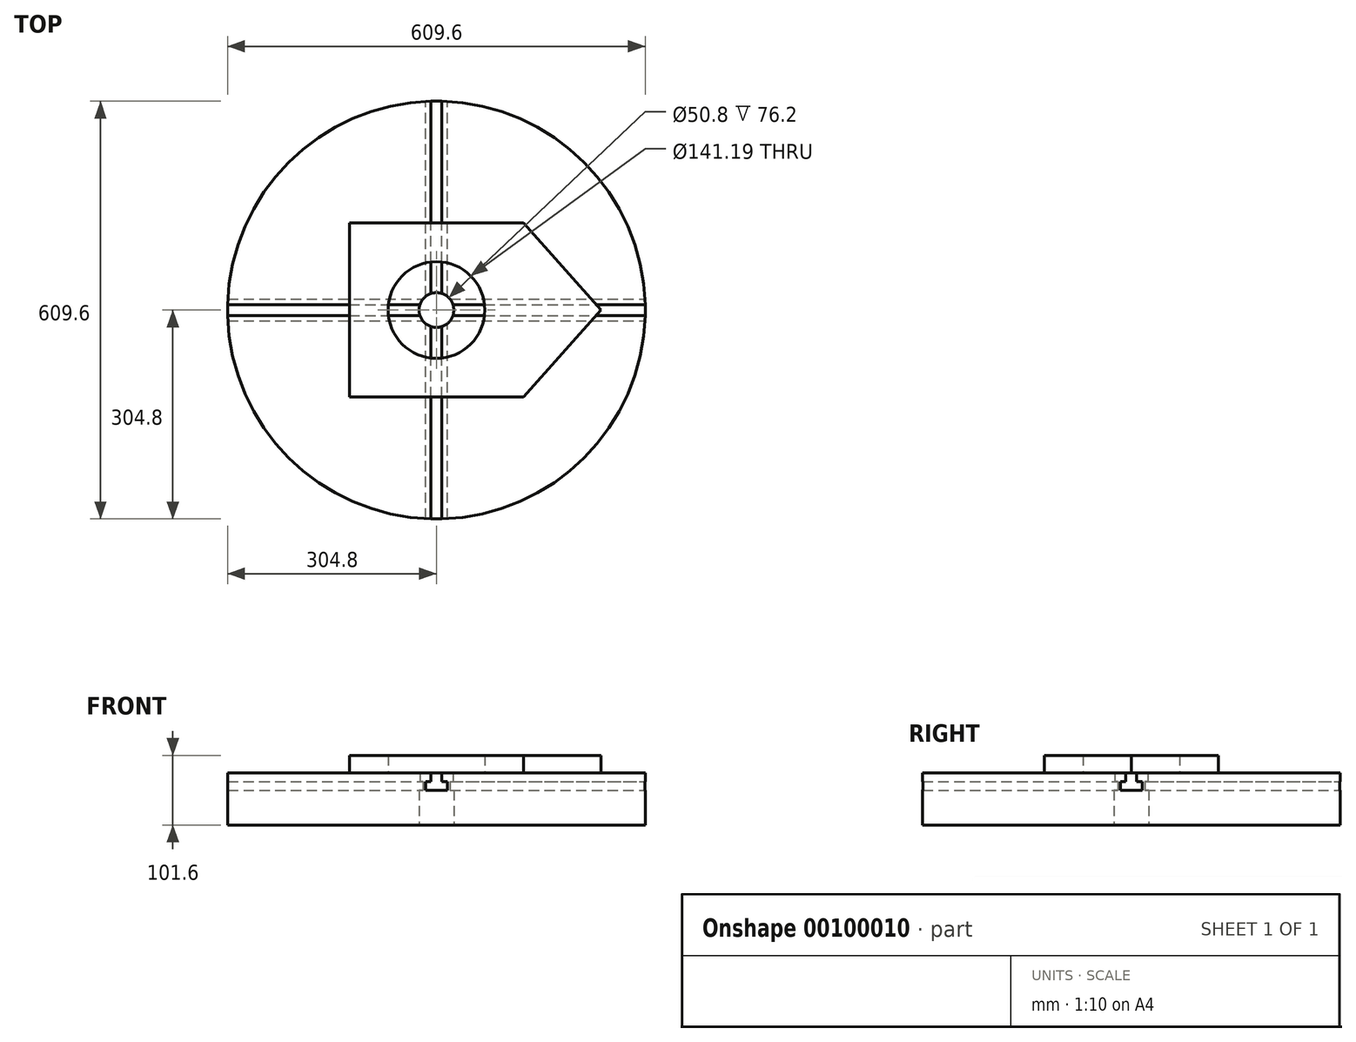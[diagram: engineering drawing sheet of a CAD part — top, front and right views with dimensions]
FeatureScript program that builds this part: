
annotation { "Feature Type Name" : "Feature", "Feature Type Description" : "" }
export const myFeature = defineFeature(function(context is Context, id is Id, definition is map)
    precondition{}
    {
        {
            var Q0;
            Q0=qCreatedBy(makeId("Top.planeOp"),FACE);
            var sketch = newSketch(context, id + "F0", { "sketchPlane" : qUnion([Q0])});
            skCircle(sketch, "E0", {"center": v(0, 0) * mm, "radius": 304.8 * mm});
            skCircle(sketch, "E1", {"center": v(0, 0) * mm, "radius": 25.4 * mm});
            skSolve(sketch);
        }
        {
            var Q0;
            Q0=qSketchRegion(id+"F0",true);
            extrude(context, id + "F1", {"entities" : qUnion([Q0]), "depth" : 76.2 * mm});
        }
        {
            var Q0;
            Q0=qCreatedBy(makeId("Front.planeOp"),FACE);
            var sketch = newSketch(context, id + "F2", { "sketchPlane" : qUnion([Q0])});
            skLineSegment(sketch, "E2", {"start": v(-7.94, 76.2) * mm, "end": v(-7.94, 63.5) * mm});
            skLineSegment(sketch, "E3", {"start": v(-7.94, 63.5) * mm, "end": v(-15.88, 63.5) * mm});
            skLineSegment(sketch, "E4", {"start": v(-15.88, 63.5) * mm, "end": v(-15.88, 50.8) * mm});
            skLineSegment(sketch, "E5", {"start": v(-15.88, 50.8) * mm, "end": v(15.88, 50.8) * mm});
            skLineSegment(sketch, "E6", {"start": v(15.88, 50.8) * mm, "end": v(15.88, 63.5) * mm});
            skLineSegment(sketch, "E7", {"start": v(15.88, 63.5) * mm, "end": v(7.94, 63.5) * mm});
            skLineSegment(sketch, "E8", {"start": v(7.94, 63.5) * mm, "end": v(7.94, 76.2) * mm});
            skLineSegment(sketch, "E9", {"start": v(7.94, 76.2) * mm, "end": v(-7.94, 76.2) * mm});
            skLineSegment(sketch, "E10", {"start": v(0, 0) * mm, "end": v(0, 117.73) * mm, "construction": true});
            skSolve(sketch);
        }
        {
            var Q0;
            Q0=makeQuery(id+"F2.imprint","IMPRINT",FACE,{"disambiguationData":[TD([[makeQuery(id+"F2.imprint","IMPRINT",EDGE,{"derivedFrom":sQuery(id+"F2.wireOp",EDGE,"E2")}),1.0]])]});
            extrude(context, id + "F3", {"entities" : qUnion([Q0]), "endBound" : BoundingType.THROUGH_ALL, "depth" : 25.4 * mm, "hasSecondDirection" : true, "secondDirectionBound" : SecondDirectionBoundingType.THROUGH_ALL, "secondDirectionOppositeDirection" : true, "secondDirectionDepth" : 25.4 * mm});
        }
        {
            var Q0;
            Q0=makeQuery(id+"F3.opExtrude","SWEPT_BODY",BODY,{"disambiguationData":[OSD([sQuery(id+"F2.wireOp",EDGE,"E2"),sQuery(id+"F2.wireOp",EDGE,"E3"),sQuery(id+"F2.wireOp",EDGE,"E4"),sQuery(id+"F2.wireOp",EDGE,"E5"),sQuery(id+"F2.wireOp",EDGE,"E6"),sQuery(id+"F2.wireOp",EDGE,"E7"),sQuery(id+"F2.wireOp",EDGE,"E8"),sQuery(id+"F2.wireOp",EDGE,"E9")])]});
            var Q1;
            Q1=sQuery(id+"F2.wireOp",EDGE,"E10");
            circularPattern(context, id + "F4", {"entities" : qUnion([Q0]), "axis" : qUnion([Q1]), "angle" : 90 * degree, "instanceCount" : 2});
        }
        {
            var Q0;
            Q0=makeQuery(id+"F4.opPattern","COPY",BODY,{"derivedFrom":makeQuery(id+"F3.opExtrude","SWEPT_BODY",BODY,{"disambiguationData":[OSD([sQuery(id+"F2.wireOp",EDGE,"E2"),sQuery(id+"F2.wireOp",EDGE,"E3"),sQuery(id+"F2.wireOp",EDGE,"E4"),sQuery(id+"F2.wireOp",EDGE,"E5"),sQuery(id+"F2.wireOp",EDGE,"E6"),sQuery(id+"F2.wireOp",EDGE,"E7"),sQuery(id+"F2.wireOp",EDGE,"E8"),sQuery(id+"F2.wireOp",EDGE,"E9")])]}),"instanceName":"1"});
            var Q1;
            Q1=makeQuery(id+"F3.opExtrude","SWEPT_BODY",BODY,{"disambiguationData":[OSD([sQuery(id+"F2.wireOp",EDGE,"E2"),sQuery(id+"F2.wireOp",EDGE,"E3"),sQuery(id+"F2.wireOp",EDGE,"E4"),sQuery(id+"F2.wireOp",EDGE,"E5"),sQuery(id+"F2.wireOp",EDGE,"E6"),sQuery(id+"F2.wireOp",EDGE,"E7"),sQuery(id+"F2.wireOp",EDGE,"E8"),sQuery(id+"F2.wireOp",EDGE,"E9")])]});
            var Q2;
            Q2=makeQuery(id+"F4.opPattern","COPY",BODY,{"derivedFrom":makeQuery(id+"F3.opExtrude","SWEPT_BODY",BODY,{"disambiguationData":[OSD([sQuery(id+"F2.wireOp",EDGE,"E2"),sQuery(id+"F2.wireOp",EDGE,"E3"),sQuery(id+"F2.wireOp",EDGE,"E4"),sQuery(id+"F2.wireOp",EDGE,"E5"),sQuery(id+"F2.wireOp",EDGE,"E6"),sQuery(id+"F2.wireOp",EDGE,"E7"),sQuery(id+"F2.wireOp",EDGE,"E8"),sQuery(id+"F2.wireOp",EDGE,"E9")])]}),"instanceName":"2"});
            var Q3;
            Q3=makeQuery(id+"F1.opExtrude","SWEPT_BODY",BODY,{"disambiguationData":[OSD([sQuery(id+"F0.wireOp",EDGE,"E0"),sQuery(id+"F0.wireOp",EDGE,"E1")])]});
            booleanBodies(context, id + "F5", {"operationType" : BooleanOperationType.SUBTRACTION, "tools" : qUnion([Q0, Q1, Q2]), "targets" : qUnion([Q3])});
        }
        {
            var Q0;
            {var subQ0=sQuery(id+"F0.wireOp",EDGE,"E0");var subQ1=sQuery(id+"F0.wireOp",EDGE,"E1");Q0=makeQuery(id+"F5.opBoolean","SPLIT",FACE,{"disambiguationData":[TD([makeQuery(id+"F1.opExtrude","SWEPT_FACE",FACE,{"disambiguationData":[OSD([subQ0])]}),makeQuery(id+"F1.opExtrude","SWEPT_FACE",FACE,{"disambiguationData":[OSD([subQ1])]}),makeQuery(id+"F3.opExtrude","SWEPT_FACE",FACE,{"disambiguationData":[OSD([sQuery(id+"F2.wireOp",EDGE,"E2")])]}),makeQuery(id+"F4.opPattern","COPY",FACE,{"derivedFrom":makeQuery(id+"F3.opExtrude","SWEPT_FACE",FACE,{"disambiguationData":[OSD([sQuery(id+"F2.wireOp",EDGE,"E8")])]}),"instanceName":"1"})])],"derivedFrom":makeQuery(id+"F1.opExtrude","CAP_FACE",FACE,{"disambiguationData":[OSD([subQ0,subQ1])],"isStart":false})});}
            var sketch = newSketch(context, id + "F6", { "sketchPlane" : qUnion([Q0])});
            skLineSegment(sketch, "E11.bottom", {"start": v(-127, 127) * mm, "end": v(127, 127) * mm});
            skLineSegment(sketch, "E11.top", {"start": v(-127, -127) * mm, "end": v(127, -127) * mm});
            skLineSegment(sketch, "E11.left", {"start": v(-127, 127) * mm, "end": v(-127, -127) * mm});
            skLineSegment(sketch, "E11.right", {"start": v(127, 127) * mm, "end": v(127, -127) * mm});
            skPoint(sketch, "E11.middle", {"position": v(0, 0) * mm});
            skLineSegment(sketch, "E12", {"start": v(-127, 127) * mm, "end": v(0, 240.08) * mm});
            skLineSegment(sketch, "E13", {"start": v(0, 240.08) * mm, "end": v(127, 127) * mm});
            skCircle(sketch, "E14", {"center": v(0, 0) * mm, "radius": 70.6 * mm});
            skSolve(sketch);
        }
        {
            var Q0;
            {var subQ1=sQuery(id+"F6.wireOp",EDGE,"E11.top");Q0=makeQuery(id+"F6.imprint","IMPRINT",FACE,{"disambiguationData":[TD([[makeQuery(id+"F6.imprint","IMPRINT",EDGE,{"derivedFrom":subQ1}),1.0]])]});}
            var Q1;
            {var subQ0=sQuery(id+"F6.wireOp",EDGE,"E11.left");var subQ8=sQuery(id+"F6.wireOp",EDGE,"E11.bottom");var subQ9=makeQuery(id+"F6.imprint","INTERSECT",VERTEX,{"derivedFrom":[subQ8,subQ0,sQuery(id+"F6.wireOp",EDGE,"E12")]});Q1=makeQuery(id+"F6.imprint","IMPRINT",FACE,{"disambiguationData":[TD([[makeQuery(id+"F6.imprint","IMPRINT",EDGE,{"disambiguationData":[TD([[subQ9,-1.0]])],"derivedFrom":subQ8}),-1.0]])]});}
            var Q2;
            {var subQ0=sQuery(id+"F6.wireOp",EDGE,"E12");var subQ1=sQuery(id+"F6.wireOp",EDGE,"E11.bottom");var subQ2=makeQuery(id+"F6.imprint","INTERSECT",VERTEX,{"derivedFrom":[subQ1,sQuery(id+"F6.wireOp",EDGE,"E11.left"),subQ0]});Q2=makeQuery(id+"F6.imprint","IMPRINT",FACE,{"disambiguationData":[TD([[makeQuery(id+"F6.imprint","IMPRINT",EDGE,{"disambiguationData":[TD([[subQ2,-1.0]])],"derivedFrom":subQ1}),1.0]])]});}
            var Q3;
            {var subQ0=sQuery(id+"F6.wireOp",EDGE,"E13");Q3=makeQuery(id+"F6.imprint","IMPRINT",FACE,{"disambiguationData":[TD([[makeQuery(id+"F6.imprint","IMPRINT",EDGE,{"derivedFrom":subQ0}),-1.0]])]});}
            extrude(context, id + "F7", {"entities" : qUnion([Q0, Q1, Q2, Q3]), "depth" : 25.4 * mm});
        }
        {
            var Q0;
            Q0=makeQuery(id+"F1.opExtrude","SWEPT_BODY",BODY,{"disambiguationData":[OSD([sQuery(id+"F0.wireOp",EDGE,"E0"),sQuery(id+"F0.wireOp",EDGE,"E1")])]});
            var Q1;
            Q1=makeQuery(id+"F7.opExtrude","SWEPT_BODY",BODY,{"disambiguationData":[OSD([sQuery(id+"F6.wireOp",EDGE,"E11.top"),sQuery(id+"F6.wireOp",EDGE,"E11.left"),sQuery(id+"F6.wireOp",EDGE,"E11.right"),sQuery(id+"F6.wireOp",EDGE,"E12"),sQuery(id+"F6.wireOp",EDGE,"E13"),sQuery(id+"F6.wireOp",EDGE,"E14")])]});
            var Q2;
            Q2=sQuery(id+"F2.wireOp",EDGE,"E10");
            transform(context, id + "F8", {"entities" : qUnion([Q0, Q1]), "transformType" : TransformType.ROTATION, "transformAxis" : qUnion([Q2]), "angle" : 90 * degree, "oppositeDirection" : true, "makeCopy" : false});
        }
    });
